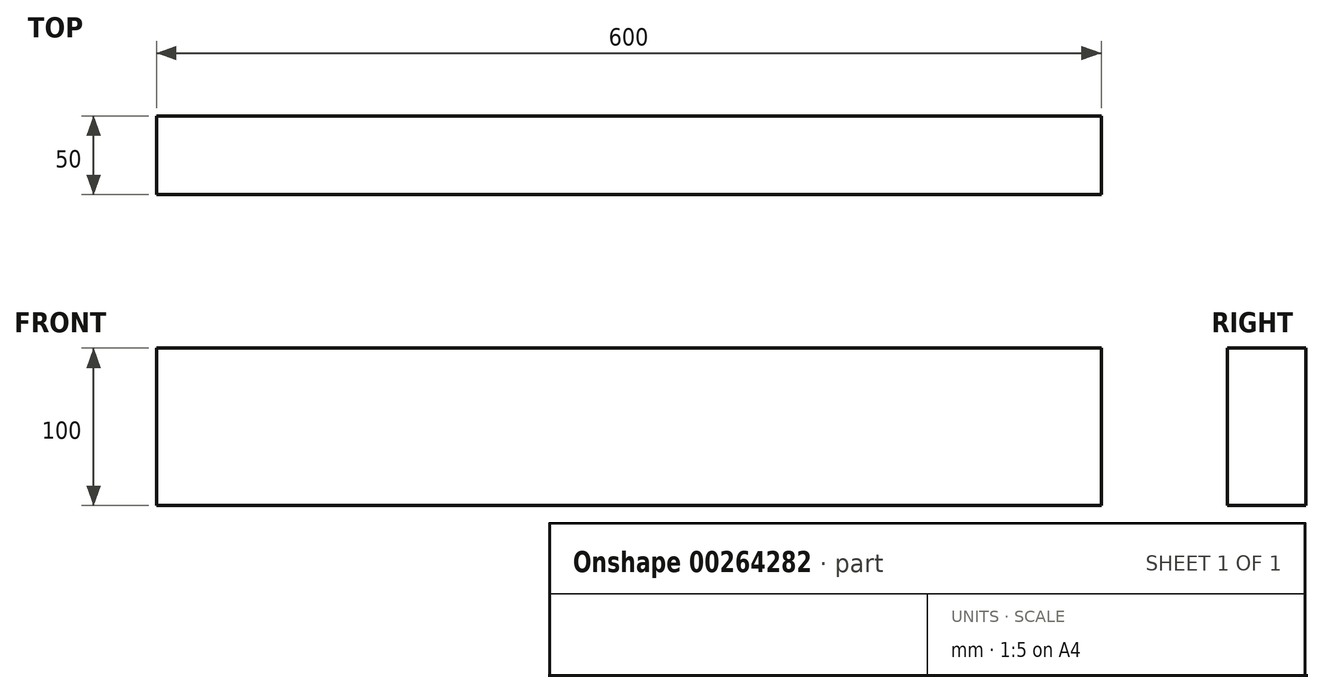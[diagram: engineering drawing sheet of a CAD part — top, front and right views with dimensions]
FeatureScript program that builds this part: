
annotation { "Feature Type Name" : "Feature", "Feature Type Description" : "" }
export const myFeature = defineFeature(function(context is Context, id is Id, definition is map)
    precondition{}
    {
        {
            var Q0;
            Q0=qCreatedBy(makeId("Front.planeOp"),FACE);
            var sketch = newSketch(context, id + "F0", { "sketchPlane" : qUnion([Q0])});
            skLineSegment(sketch, "E0.bottom", {"start": v(-300, 50) * mm, "end": v(300, 50) * mm});
            skLineSegment(sketch, "E0.top", {"start": v(-300, -50) * mm, "end": v(300, -50) * mm});
            skLineSegment(sketch, "E0.left", {"start": v(-300, 50) * mm, "end": v(-300, -50) * mm});
            skLineSegment(sketch, "E0.right", {"start": v(300, 50) * mm, "end": v(300, -50) * mm});
            skLineSegment(sketch, "E1", {"start": v(-300, 0) * mm, "end": v(300, 0) * mm, "construction": true});
            skLineSegment(sketch, "E2", {"start": v(0, 50) * mm, "end": v(0, -50) * mm, "construction": true});
            skSolve(sketch);
        }
        {
            var Q0;
            Q0=makeQuery(id+"F0.imprint","IMPRINT",FACE,{"disambiguationData":[TD([[makeQuery(id+"F0.imprint","IMPRINT",EDGE,{"derivedFrom":sQuery(id+"F0.wireOp",EDGE,"E0.bottom")}),-1.0]])]});
            extrude(context, id + "F1", {"entities" : qUnion([Q0]), "endBound" : BoundingType.SYMMETRIC, "depth" : 50 * mm});
        }
    });
